# Revit family: Korobka raspredelitelnaya KR60kh60kh30
name_source: partatom
category: Датчики
units: mm (PartAtom-declared; Revit-internal decimal feet)

## family parameters
Всегда вертикально = Да
Заголовок OmniClass = Electric Power and Lighting
На основе рабочей плоскости = Нет
Номер OmniClass = 23.80.00.00
Общий = Нет
При загрузке вырезать с полостями = Нет
Размер круглого соединителя = Использовать диаметр
Сохранять ориентацию аннотаций = Нет
Тип детали = Нормальный
Точка принадлежности помещению = Нет

## types (2) — shared parameters
ADSK_Единица измерения = шт.
ADSK_Завод-изготовитель = ООО НПП «МАГНИТО-КОНТАКТ»
ADSK_Масса = 0.2
ADSK_Материал = Пластик белый
ADSK_Наименование = Коробка распределительная КР60х60х30 IP65
ADSK_Обозначение = АТФЕ.685552.178
ADSK_Примечание = Степень защиты от внешних воздействий по ГОСТ 14254 IP65
ADSK_Размер_Высота = 30 мм
URL = https://m-kontakt.ru
Изготовитель = ООО НПП "Магнито-Контакт"
Метизы = Металл
Описание = Коробка распределительная КР60х60х30, IP65 предназначена для соединения (разветвления) электрических проводок сигнальных кабелей, например в шлейфах сигнализации, линиях связи и телекоммуникаций, цепях в системах управления и автоматики, а также подключения в шлейфы оконечных устройств и т.п.
Срок службы = не менее 10 лет
Условия эксплуатации = Температура окружающей среды от -60°С до +85°С, относительная влажность не более 93% при температуре 40°С
zero-valued in all types: Отметка по умолчанию

## per-type parameters (varying)
| type | ADSK_Размер_Длина | ADSK_Размер_Ширина | Кабельные вводы |
| Коробка распределительная КР60х60х30 | 60 мм | 60 мм | Нет |
| Коробка распределительная КР60х60х30 с кабельными вводами | 106 мм | 106 мм | Да |
